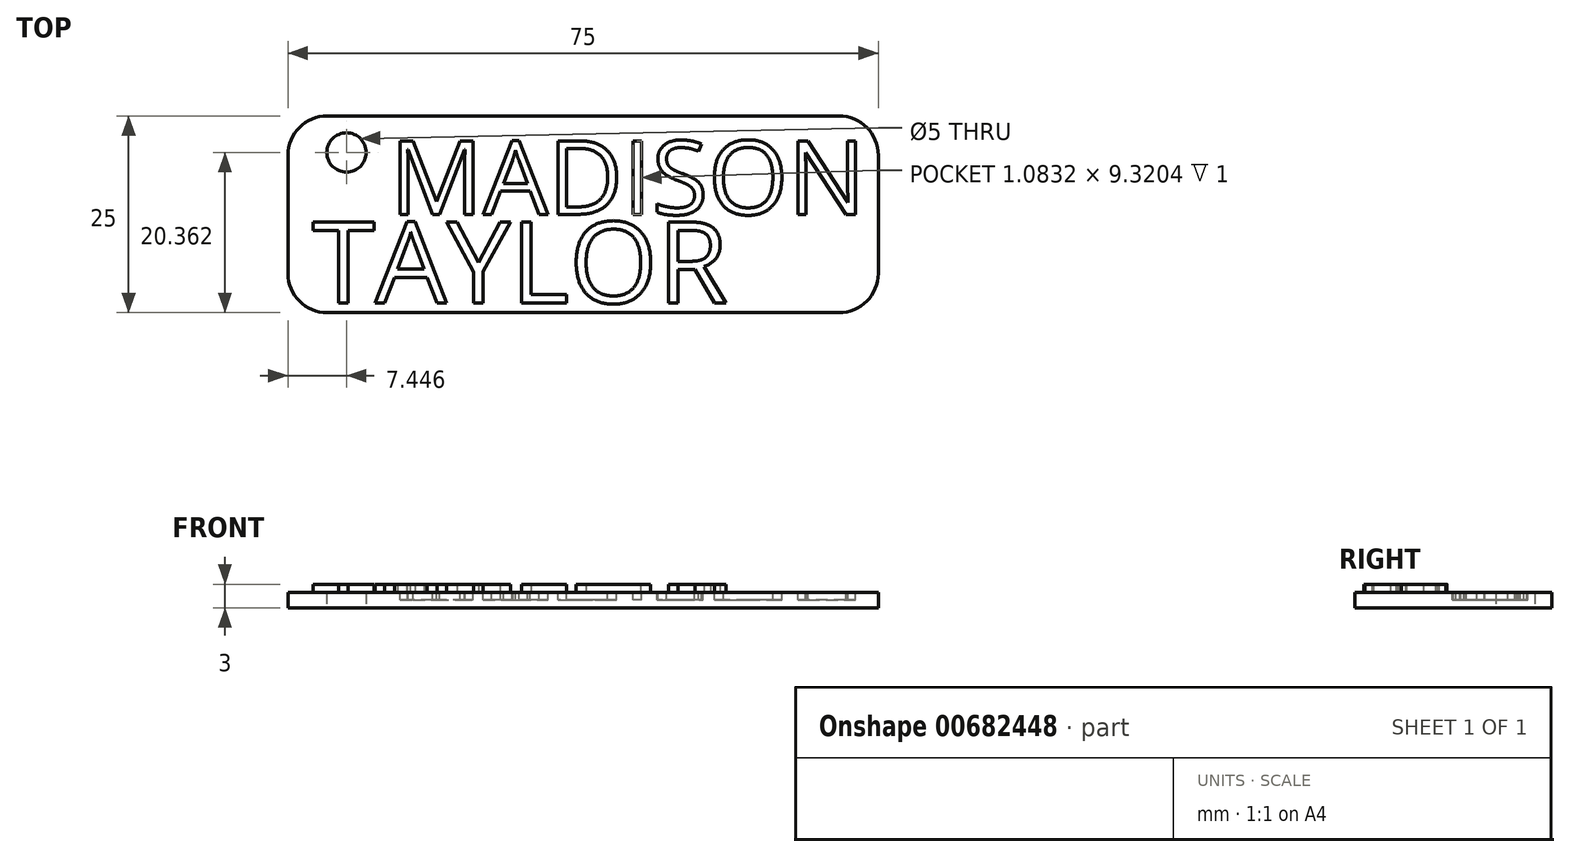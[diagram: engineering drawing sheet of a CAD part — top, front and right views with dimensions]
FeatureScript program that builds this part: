
annotation { "Feature Type Name" : "Feature", "Feature Type Description" : "" }
export const myFeature = defineFeature(function(context is Context, id is Id, definition is map)
    precondition{}
    {
        {
            var Q0;
            Q0=qCreatedBy(makeId("Top.planeOp"),FACE);
            var sketch = newSketch(context, id + "F0", { "sketchPlane" : qUnion([Q0])});
            skLineSegment(sketch, "E0.bottom", {"start": v(32.5, 12.5) * mm, "end": v(-32.5, 12.5) * mm});
            skLineSegment(sketch, "E0.top", {"start": v(32.5, -12.5) * mm, "end": v(-32.5, -12.5) * mm});
            skLineSegment(sketch, "E0.left", {"start": v(37.5, 7.5) * mm, "end": v(37.5, -7.5) * mm});
            skLineSegment(sketch, "E0.right", {"start": v(-37.5, 7.5) * mm, "end": v(-37.5, -7.5) * mm});
            skPoint(sketch, "E0.middle", {"position": v(0, 0) * mm});
            skPoint(sketch, "E1.visualSharp", {"position": v(-37.5, 12.5) * mm});
            skArc(sketch, "E1.filletArc", {"start": v(-32.5, 12.5) * mm, "mid": v(-36.04, 11.04) * mm, "end": v(-37.5, 7.5) * mm});
            skPoint(sketch, "E2.visualSharp", {"position": v(-37.5, -12.5) * mm});
            skArc(sketch, "E2.filletArc", {"start": v(-37.5, -7.5) * mm, "mid": v(-36.04, -11.04) * mm, "end": v(-32.5, -12.5) * mm});
            skPoint(sketch, "E3.visualSharp", {"position": v(37.5, 12.5) * mm});
            skArc(sketch, "E3.filletArc", {"start": v(37.5, 7.5) * mm, "mid": v(36.04, 11.04) * mm, "end": v(32.5, 12.5) * mm});
            skPoint(sketch, "E4.visualSharp", {"position": v(37.5, -12.5) * mm});
            skArc(sketch, "E4.filletArc", {"start": v(32.5, -12.5) * mm, "mid": v(36.04, -11.04) * mm, "end": v(37.5, -7.5) * mm});
            skSolve(sketch);
        }
        {
            var Q0;
            Q0=makeQuery(id+"F0.imprint","IMPRINT",FACE,{"disambiguationData":[TD([[makeQuery(id+"F0.imprint","IMPRINT",EDGE,{"derivedFrom":sQuery(id+"F0.wireOp",EDGE,"E0.bottom")}),1.0]])]});
            extrude(context, id + "F1", {"entities" : qUnion([Q0]), "depth" : 2 * mm, "offsetDistance" : 25 * mm});
        }
        {
            var Q0;
            Q0=qCreatedBy(makeId("Top.planeOp"),FACE);
            var sketch = newSketch(context, id + "F2", { "sketchPlane" : qUnion([Q0])});
            skPoint(sketch, "E5", {"position": v(-30.05, 7.86) * mm});
            skSolve(sketch);
        }
        {
            var Q0;
            Q0=sQuery(id+"F2.wireOp",VERTEX,"E5");
            var Q1;
            Q1=makeQuery(id+"F1.opExtrude","SWEPT_BODY",BODY,{"disambiguationData":[OSD([sQuery(id+"F0.wireOp",EDGE,"E0.bottom"),sQuery(id+"F0.wireOp",EDGE,"E0.top"),sQuery(id+"F0.wireOp",EDGE,"E0.left"),sQuery(id+"F0.wireOp",EDGE,"E0.right"),sQuery(id+"F0.wireOp",EDGE,"E1.filletArc"),sQuery(id+"F0.wireOp",EDGE,"E2.filletArc"),sQuery(id+"F0.wireOp",EDGE,"E3.filletArc"),sQuery(id+"F0.wireOp",EDGE,"E4.filletArc")])]});
            hole(context, id + "F3", {"style" : HoleStyle.SIMPLE, "endStyle" : HoleEndStyle.THROUGH, "oppositeDirection" : true, "holeDiameter" : 5 * mm, "majorDiameter" : 5 * mm, "isTappedThrough" : true, "tappedDepth" : 12 * mm, "tapClearance" : 3, "locations" : qUnion([Q0]), "scope" : qUnion([Q1])});
        }
        {
            var Q0;
            Q0=makeQuery(id+"F1.opExtrude","CAP_FACE",FACE,{"disambiguationData":[OSD([sQuery(id+"F0.wireOp",EDGE,"E0.bottom"),sQuery(id+"F0.wireOp",EDGE,"E0.top"),sQuery(id+"F0.wireOp",EDGE,"E0.left"),sQuery(id+"F0.wireOp",EDGE,"E0.right"),sQuery(id+"F0.wireOp",EDGE,"E1.filletArc"),sQuery(id+"F0.wireOp",EDGE,"E2.filletArc"),sQuery(id+"F0.wireOp",EDGE,"E3.filletArc"),sQuery(id+"F0.wireOp",EDGE,"E4.filletArc")])],"isStart":false});
            var sketch = newSketch(context, id + "F4", { "sketchPlane" : qUnion([Q0])});
            skText(sketch, "E6", { "text": "MADISON", "fontName": "OpenSans-Regular.ttf"});
            const initialGuessF4  = {"E6": [-0.0245, 0, 1, 0, 0.0094]};
            skSetInitialGuess(sketch, initialGuessF4);
            skSolve(sketch);
        }
        {
            var Q0;
            Q0=makeQuery(id+"F4.imprint","IMPRINT",FACE,{"disambiguationData":[TD([[makeQuery(id+"F4.imprint","IMPRINT",EDGE,{"derivedFrom":sQuery(id+"F4.wireOp",EDGE,"E6.sketch_text.stroke-0")}),1.0]])]});
            var sketch = newSketch(context, id + "F5", { "sketchPlane" : qUnion([Q0])});
            skText(sketch, "E7", { "text": "TAYLOR", "fontName": "OpenSans-Regular.ttf"});
            const initialGuessF5  = {"E7": [-0.03442, -0.01127, 1, 0, 0.01038]};
            skSetInitialGuess(sketch, initialGuessF5);
            skSolve(sketch);
        }
        {
            var Q0;
            Q0 = qSketchRegion(id + "F5", true);
            extrude(context, id + "F6", {"entities" : qUnion([Q0]), "operationType" : NewBodyOperationType.ADD, "depth" : 1 * mm, "offsetDistance" : 25 * mm});
        }
        {
            var Q0;
            Q0 = qSketchRegion(id + "F4", true);
            extrude(context, id + "F7", {"entities" : qUnion([Q0]), "operationType" : NewBodyOperationType.REMOVE, "oppositeDirection" : true, "depth" : 1 * mm, "offsetDistance" : 25 * mm});
        }
    });
